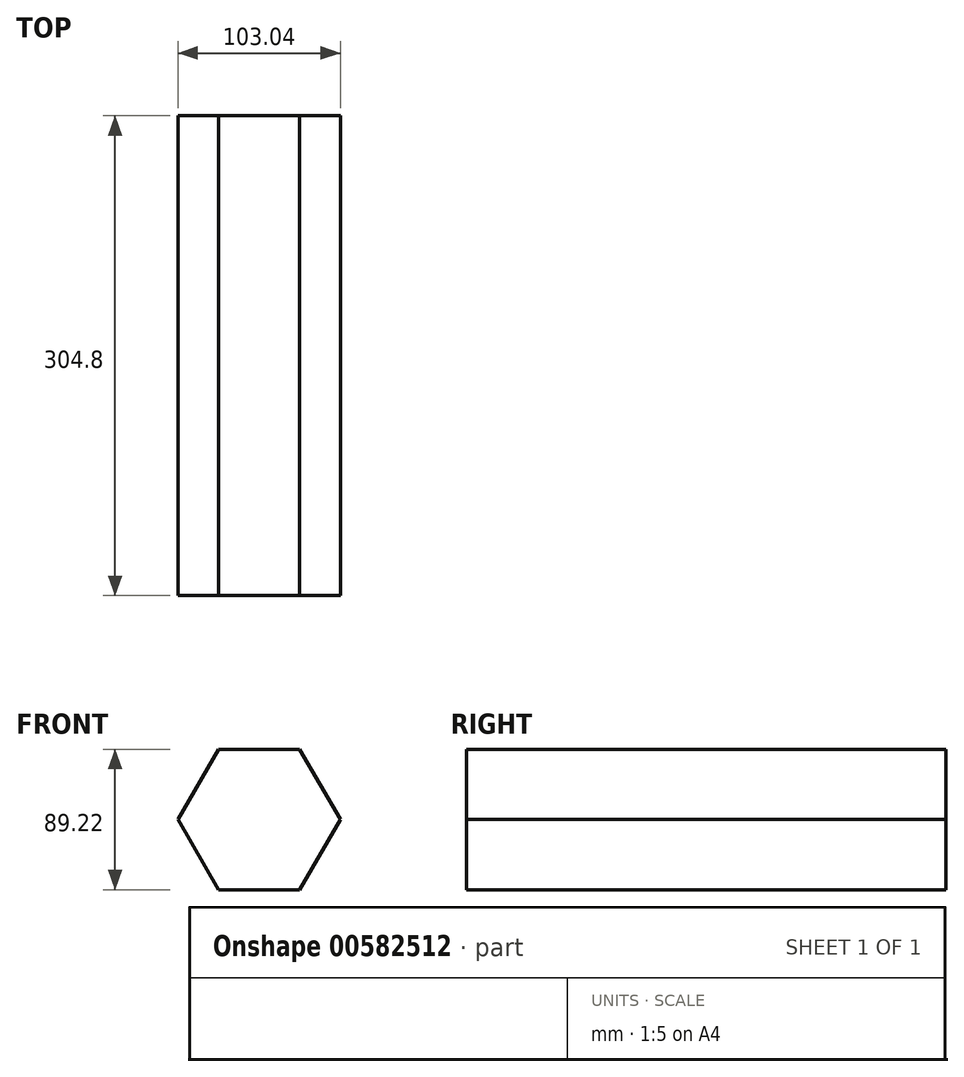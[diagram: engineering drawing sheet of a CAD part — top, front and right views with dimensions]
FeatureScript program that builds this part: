
annotation { "Feature Type Name" : "Feature", "Feature Type Description" : "" }
export const myFeature = defineFeature(function(context is Context, id is Id, definition is map)
    precondition{}
    {
        {
            var Q0;
            Q0=qCreatedBy(makeId("Front.planeOp"),FACE);
            var sketch = newSketch(context, id + "F0", { "sketchPlane" : qUnion([Q0])});
            skCircle(sketch, "E0.cCircle", {"center": v(0, 0) * mm, "radius": 44.61 * mm, "construction": true});
            skLineSegment(sketch, "E0.0", {"start": v(-25.76, 44.61) * mm, "end": v(25.76, 44.61) * mm});
            skLineSegment(sketch, "E0.1", {"start": v(25.76, 44.61) * mm, "end": v(51.52, 0) * mm});
            skLineSegment(sketch, "E0.2", {"start": v(51.52, 0) * mm, "end": v(25.76, -44.61) * mm});
            skLineSegment(sketch, "E0.3", {"start": v(25.76, -44.61) * mm, "end": v(-25.76, -44.61) * mm});
            skLineSegment(sketch, "E0.4", {"start": v(-25.76, -44.61) * mm, "end": v(-51.52, 0) * mm});
            skLineSegment(sketch, "E0.5", {"start": v(-51.52, 0) * mm, "end": v(-25.76, 44.61) * mm});
            skPoint(sketch, "E0.0.midPoint", {"position": v(0, 44.61) * mm});
            skCircle(sketch, "E1", {"center": v(0, 0) * mm, "radius": 28.75 * mm});
            skSolve(sketch);
        }
        {
            var Q0;
            Q0=makeQuery(id+"F0.imprint","IMPRINT",FACE,{"disambiguationData":[TD([[makeQuery(id+"F0.imprint","IMPRINT",EDGE,{"derivedFrom":sQuery(id+"F0.wireOp",EDGE,"E0.0")}),-1.0]])]});
            var Q1;
            Q1=makeQuery(id+"F0.imprint","IMPRINT",FACE,{"disambiguationData":[TD([[makeQuery(id+"F0.imprint","IMPRINT",EDGE,{"derivedFrom":sQuery(id+"F0.wireOp",EDGE,"E1")}),1.0]])]});
            extrude(context, id + "F1", {"entities" : qUnion([Q0, Q1]), "depth" : 304.8 * mm, "offsetDistance" : 25.4 * mm});
        }
    });
